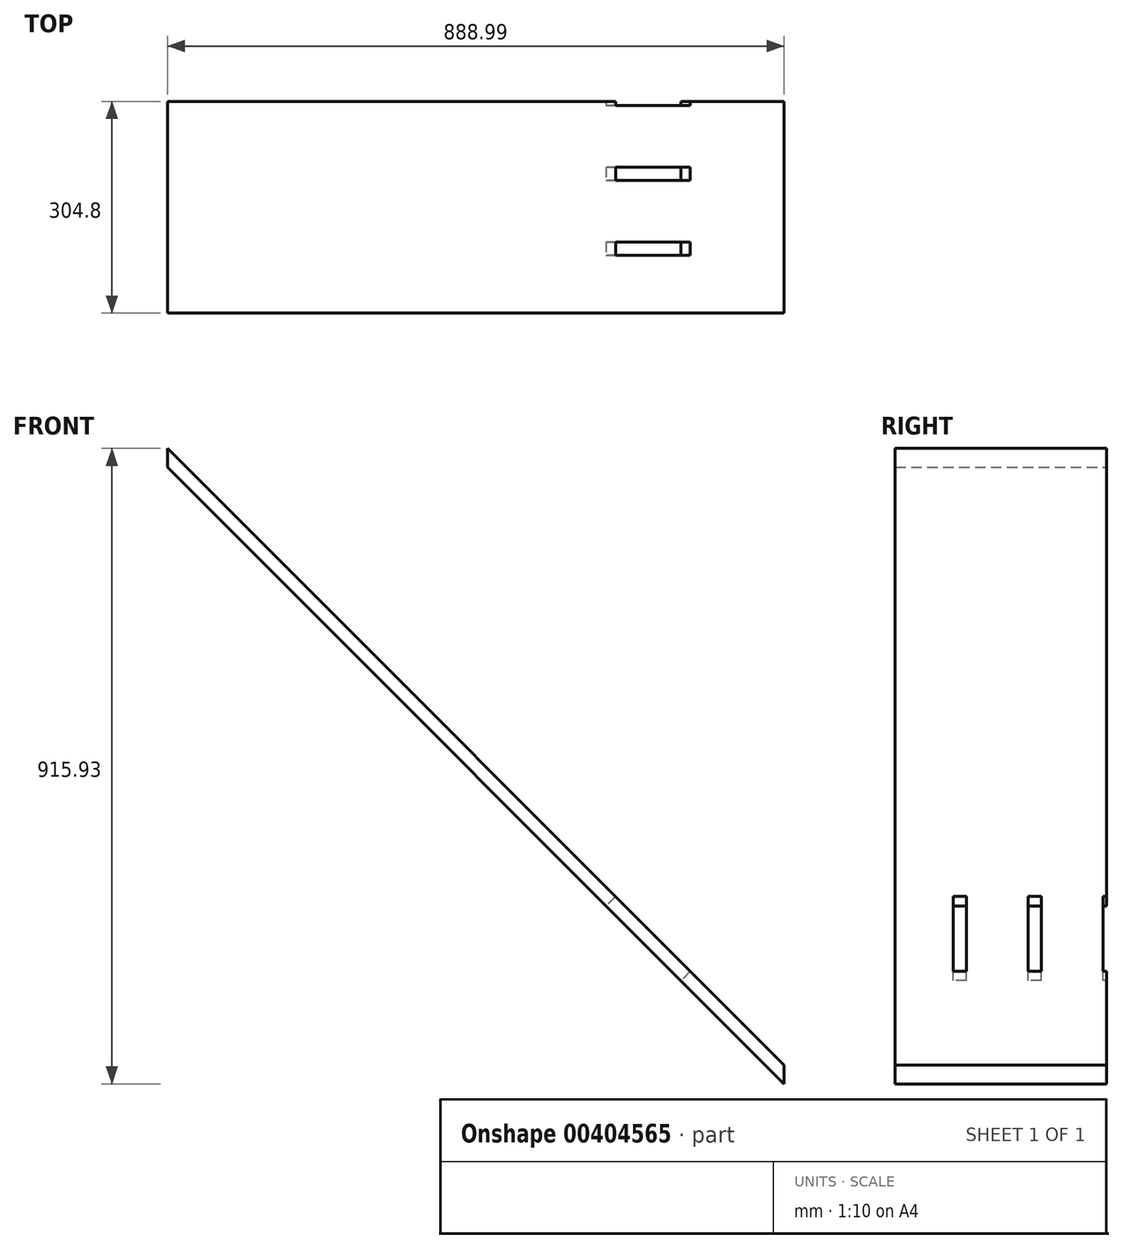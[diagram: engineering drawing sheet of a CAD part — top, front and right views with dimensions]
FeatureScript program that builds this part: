
annotation { "Feature Type Name" : "Feature", "Feature Type Description" : "" }
export const myFeature = defineFeature(function(context is Context, id is Id, definition is map)
    precondition{}
    {
        {
            var Q0;
            Q0=qCreatedBy(makeId("Front.planeOp"),FACE);
            var sketch = newSketch(context, id + "F0", { "sketchPlane" : qUnion([Q0])});
            skLineSegment(sketch, "E0.right", {"start": v(-375.81, 889) * mm, "end": v(-375.81, 915.93) * mm});
            skLineSegment(sketch, "E1.MirrorCS", {"start": v(513.18, 0) * mm, "end": v(-375.81, 889) * mm});
            skLineSegment(sketch, "E2.MirrorCS", {"start": v(513.18, 26.94) * mm, "end": v(-375.81, 915.93) * mm});
            skLineSegment(sketch, "E3.MirrorCS", {"start": v(513.18, 0) * mm, "end": v(513.18, 26.94) * mm});
            skSolve(sketch);
        }
        {
            var Q0;
            Q0=qSketchRegion(id+"F0",true);
            extrude(context, id + "F1", {"entities" : qUnion([Q0]), "endBound" : BoundingType.SYMMETRIC, "depth" : 304.8 * mm});
        }
        {
            var Q0;
            Q0=makeQuery(id+"F1.opExtrude","SWEPT_FACE",FACE,{"disambiguationData":[OSD([sQuery(id+"F0.wireOp",EDGE,"E2.MirrorCS")])]});
            var sketch = newSketch(context, id + "F2", { "sketchPlane" : qUnion([Q0])});
            skLineSegment(sketch, "E4.bottom", {"start": v(273.97, -152.4) * mm, "end": v(254.92, -152.4) * mm});
            skLineSegment(sketch, "E4.top", {"start": v(273.97, 0) * mm, "end": v(254.92, 0) * mm});
            skLineSegment(sketch, "E4.left", {"start": v(273.97, -152.4) * mm, "end": v(273.97, 0) * mm});
            skLineSegment(sketch, "E4.right", {"start": v(254.92, -152.4) * mm, "end": v(254.92, 0) * mm});
            skLineSegment(sketch, "E5.bottom", {"start": v(166.02, -152.4) * mm, "end": v(146.97, -152.4) * mm});
            skLineSegment(sketch, "E5.top", {"start": v(166.02, 0) * mm, "end": v(146.97, 0) * mm});
            skLineSegment(sketch, "E5.left", {"start": v(166.02, -152.4) * mm, "end": v(166.02, 0) * mm});
            skLineSegment(sketch, "E5.right", {"start": v(146.97, -152.4) * mm, "end": v(146.97, 0) * mm});
            skLineSegment(sketch, "E6.bottom", {"start": v(58.07, -152.4) * mm, "end": v(39.02, -152.4) * mm});
            skLineSegment(sketch, "E6.top", {"start": v(58.07, 0) * mm, "end": v(39.02, 0) * mm});
            skLineSegment(sketch, "E6.left", {"start": v(58.07, -152.4) * mm, "end": v(58.07, 0) * mm});
            skLineSegment(sketch, "E6.right", {"start": v(39.02, -152.4) * mm, "end": v(39.02, 0) * mm});
            skLineSegment(sketch, "E7.bottom", {"start": v(-49.88, -152.4) * mm, "end": v(-68.93, -152.4) * mm});
            skLineSegment(sketch, "E7.top", {"start": v(-49.88, 0) * mm, "end": v(-68.93, 0) * mm});
            skLineSegment(sketch, "E7.left", {"start": v(-49.88, -152.4) * mm, "end": v(-49.88, 0) * mm});
            skLineSegment(sketch, "E7.right", {"start": v(-68.93, -152.4) * mm, "end": v(-68.93, 0) * mm});
            skLineSegment(sketch, "E8.bottom", {"start": v(-157.83, -152.4) * mm, "end": v(-176.88, -152.4) * mm});
            skLineSegment(sketch, "E8.top", {"start": v(-157.83, 0) * mm, "end": v(-176.88, 0) * mm});
            skLineSegment(sketch, "E8.left", {"start": v(-157.83, -152.4) * mm, "end": v(-157.83, 0) * mm});
            skLineSegment(sketch, "E8.right", {"start": v(-176.88, -152.4) * mm, "end": v(-176.88, 0) * mm});
            skLineSegment(sketch, "E9.bottom", {"start": v(-265.78, -152.4) * mm, "end": v(-284.83, -152.4) * mm});
            skLineSegment(sketch, "E9.top", {"start": v(-265.78, 0) * mm, "end": v(-284.83, 0) * mm});
            skLineSegment(sketch, "E9.left", {"start": v(-265.78, -152.4) * mm, "end": v(-265.78, 0) * mm});
            skLineSegment(sketch, "E9.right", {"start": v(-284.83, -152.4) * mm, "end": v(-284.83, 0) * mm});
            skLineSegment(sketch, "E10.bottom", {"start": v(-373.73, -152.4) * mm, "end": v(-392.78, -152.4) * mm});
            skLineSegment(sketch, "E10.top", {"start": v(-373.73, 0) * mm, "end": v(-392.78, 0) * mm});
            skLineSegment(sketch, "E10.left", {"start": v(-373.73, -152.4) * mm, "end": v(-373.73, 0) * mm});
            skLineSegment(sketch, "E10.right", {"start": v(-392.78, -152.4) * mm, "end": v(-392.78, 0) * mm});
            skLineSegment(sketch, "E11.bottom", {"start": v(-481.68, -152.4) * mm, "end": v(-500.73, -152.4) * mm});
            skLineSegment(sketch, "E11.top", {"start": v(-481.68, 0) * mm, "end": v(-500.73, 0) * mm});
            skLineSegment(sketch, "E11.left", {"start": v(-481.68, -152.4) * mm, "end": v(-481.68, 0) * mm});
            skLineSegment(sketch, "E11.right", {"start": v(-500.73, -152.4) * mm, "end": v(-500.73, 0) * mm});
            skLineSegment(sketch, "E12.bottom", {"start": v(-589.63, -152.4) * mm, "end": v(-608.68, -152.4) * mm});
            skLineSegment(sketch, "E12.top", {"start": v(-589.63, 0) * mm, "end": v(-608.68, 0) * mm});
            skLineSegment(sketch, "E12.left", {"start": v(-589.63, -152.4) * mm, "end": v(-589.63, 0) * mm});
            skLineSegment(sketch, "E12.right", {"start": v(-608.68, -152.4) * mm, "end": v(-608.68, 0) * mm});
            skLineSegment(sketch, "E13.bottom", {"start": v(-697.58, -152.4) * mm, "end": v(-716.63, -152.4) * mm});
            skLineSegment(sketch, "E13.top", {"start": v(-697.58, 0) * mm, "end": v(-716.63, 0) * mm});
            skLineSegment(sketch, "E13.left", {"start": v(-697.58, -152.4) * mm, "end": v(-697.58, 0) * mm});
            skLineSegment(sketch, "E13.right", {"start": v(-716.63, -152.4) * mm, "end": v(-716.63, 0) * mm});
            skLineSegment(sketch, "E14.bottom", {"start": v(-805.53, -152.4) * mm, "end": v(-824.58, -152.4) * mm});
            skLineSegment(sketch, "E14.top", {"start": v(-805.53, 0) * mm, "end": v(-824.58, 0) * mm});
            skLineSegment(sketch, "E14.left", {"start": v(-805.53, -152.4) * mm, "end": v(-805.53, 0) * mm});
            skLineSegment(sketch, "E14.right", {"start": v(-824.58, -152.4) * mm, "end": v(-824.58, 0) * mm});
            skSolve(sketch);
        }
        {
            var Q0;
            Q0=qSketchRegion(id+"F2",true);
            extrude(context, id + "F3", {"entities" : qUnion([Q0]), "operationType" : NewBodyOperationType.REMOVE, "oppositeDirection" : true, "depth" : 19.05 * mm});
        }
    });
